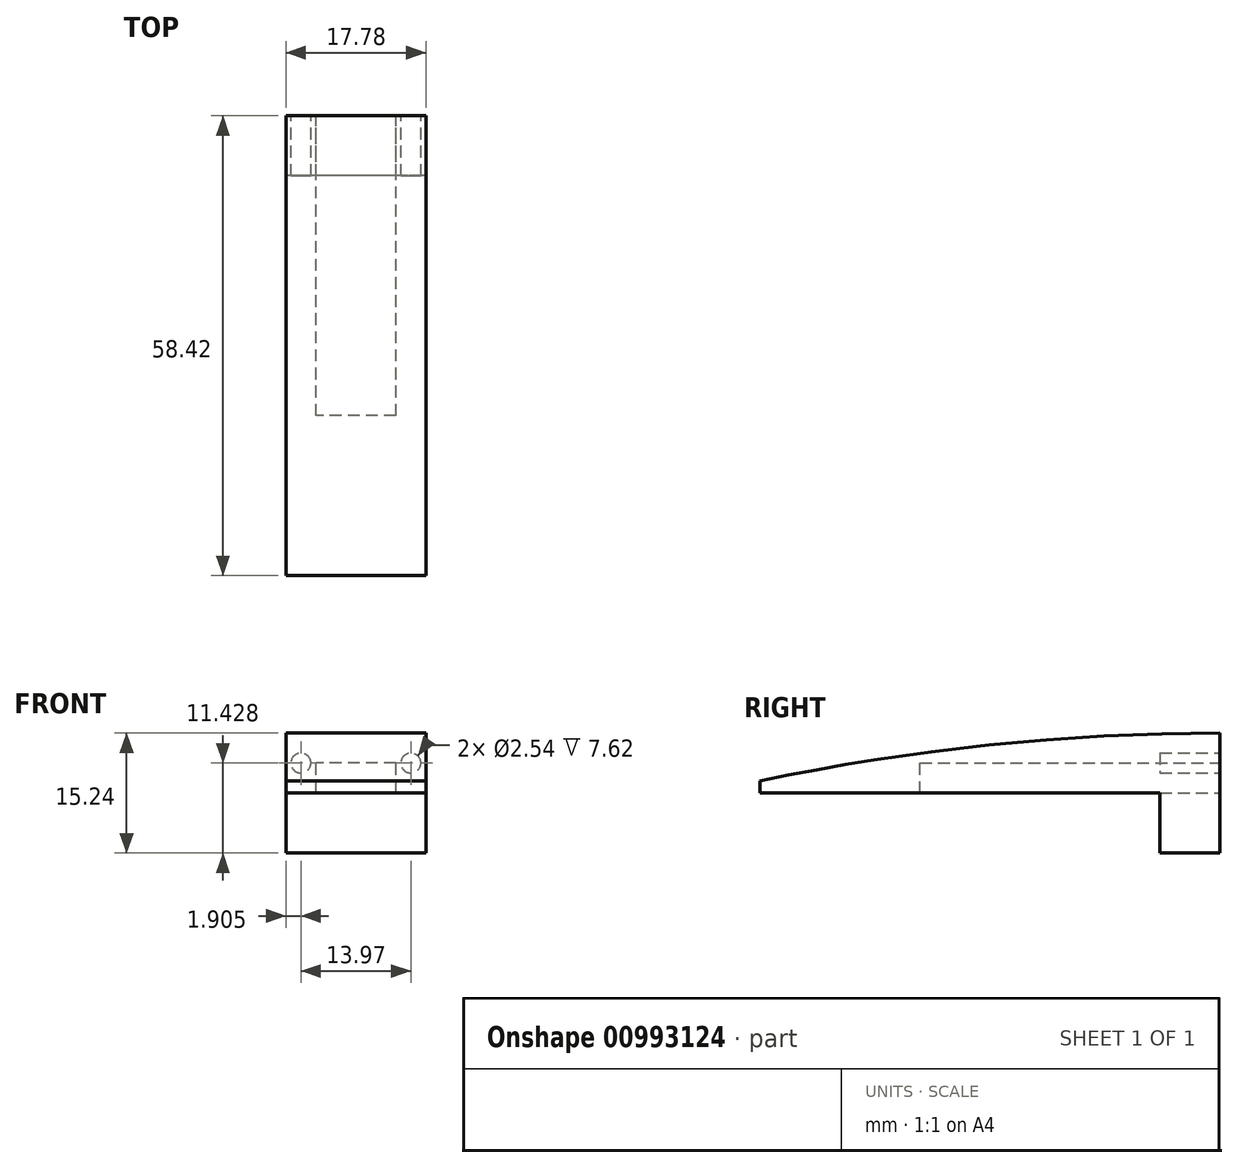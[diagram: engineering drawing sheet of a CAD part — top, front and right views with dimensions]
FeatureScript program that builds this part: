
annotation { "Feature Type Name" : "Feature", "Feature Type Description" : "" }
export const myFeature = defineFeature(function(context is Context, id is Id, definition is map)
    precondition{}
    {
        {
            var Q0;
            Q0=qCreatedBy(makeId("Right.planeOp"),FACE);
            var sketch = newSketch(context, id + "F0", { "sketchPlane" : qUnion([Q0])});
            skLineSegment(sketch, "E0.bottom", {"start": v(-45.06, 41.12) * mm, "end": v(5.74, 41.12) * mm});
            skLineSegment(sketch, "E0.top", {"start": v(-45.06, 33.5) * mm, "end": v(5.74, 33.5) * mm});
            skLineSegment(sketch, "E0.left", {"start": v(-45.06, 41.12) * mm, "end": v(-45.06, 33.5) * mm});
            skLineSegment(sketch, "E0.right", {"start": v(5.74, 41.12) * mm, "end": v(5.74, 33.5) * mm});
            skLineSegment(sketch, "E1.bottom", {"start": v(5.74, 41.12) * mm, "end": v(13.36, 41.12) * mm});
            skLineSegment(sketch, "E1.top", {"start": v(5.74, 25.88) * mm, "end": v(13.36, 25.88) * mm});
            skLineSegment(sketch, "E1.left", {"start": v(5.74, 41.12) * mm, "end": v(5.74, 25.88) * mm});
            skLineSegment(sketch, "E1.right", {"start": v(13.36, 41.12) * mm, "end": v(13.36, 25.88) * mm});
            skSolve(sketch);
        }
        {
            var Q0;
            {var subQ0=sQuery(id+"F0.wireOp",EDGE,"E0.bottom");Q0=makeQuery(id+"F0.imprint","IMPRINT",FACE,{"disambiguationData":[TD([[makeQuery(id+"F0.imprint","IMPRINT",EDGE,{"derivedFrom":subQ0}),-1.0]])]});}
            var Q1;
            {var subQ3=sQuery(id+"F0.wireOp",EDGE,"E1.bottom");Q1=makeQuery(id+"F0.imprint","IMPRINT",FACE,{"disambiguationData":[TD([[makeQuery(id+"F0.imprint","IMPRINT",EDGE,{"derivedFrom":subQ3}),-1.0]])]});}
            extrude(context, id + "F1", {"entities" : qUnion([Q0, Q1]), "depth" : 17.78 * mm, "offsetDistance" : 25.4 * mm});
        }
        {
            var Q0;
            Q0=makeQuery(id+"F1.opExtrude","CAP_FACE",FACE,{"disambiguationData":[OSD([sQuery(id+"F0.wireOp",EDGE,"E0.bottom"),sQuery(id+"F0.wireOp",EDGE,"E0.top"),sQuery(id+"F0.wireOp",EDGE,"E0.left"),sQuery(id+"F0.wireOp",EDGE,"E1.bottom"),sQuery(id+"F0.wireOp",EDGE,"E1.top"),sQuery(id+"F0.wireOp",EDGE,"E1.left"),sQuery(id+"F0.wireOp",EDGE,"E1.right")])],"isStart":false});
            var sketch = newSketch(context, id + "F2", { "sketchPlane" : qUnion([Q0])});
            skArc(sketch, "E2", {"start": v(13.36, 41.12) * mm, "mid": v(-16, 39.6) * mm, "end": v(-45.06, 35.03) * mm});
            skSolve(sketch);
        }
        {
            var Q0;
            {var subQ0=sQuery(id+"F2.wireOp",EDGE,"E2");Q0=makeQuery(id+"F2.imprint","IMPRINT",FACE,{"disambiguationData":[TD([[makeQuery(id+"F2.imprint","IMPRINT",EDGE,{"derivedFrom":subQ0}),-1.0]])]});}
            extrude(context, id + "F3", {"entities" : qUnion([Q0]), "operationType" : NewBodyOperationType.REMOVE, "oppositeDirection" : true, "depth" : 25.4 * mm, "offsetDistance" : 25.4 * mm});
        }
        {
            var Q0;
            Q0=makeQuery(id+"F1.opExtrude","SWEPT_FACE",FACE,{"disambiguationData":[OSD([sQuery(id+"F0.wireOp",EDGE,"E1.right")])]});
            var sketch = newSketch(context, id + "F4", { "sketchPlane" : qUnion([Q0])});
            skPoint(sketch, "E3.firstSnap0", {"position": v(-17.78, 33.5) * mm});
            skLineSegment(sketch, "E3.bottom", {"start": v(-13.97, 33.5) * mm, "end": v(-3.8, 33.5) * mm});
            skLineSegment(sketch, "E3.top", {"start": v(-13.97, 37.3) * mm, "end": v(-3.8, 37.3) * mm});
            skLineSegment(sketch, "E3.left", {"start": v(-13.97, 33.5) * mm, "end": v(-13.97, 37.3) * mm});
            skLineSegment(sketch, "E3.right", {"start": v(-3.8, 33.5) * mm, "end": v(-3.8, 37.3) * mm});
            skCircle(sketch, "E4", {"center": v(-15.88, 37.3) * mm, "radius": 1.27 * mm});
            skCircle(sketch, "E5", {"center": v(-1.9, 37.3) * mm, "radius": 1.27 * mm});
            skSolve(sketch);
        }
        {
            var Q0;
            Q0=makeQuery(id+"F4.imprint","IMPRINT",FACE,{"disambiguationData":[TD([[makeQuery(id+"F4.imprint","IMPRINT",EDGE,{"derivedFrom":sQuery(id+"F4.wireOp",EDGE,"E3.bottom")}),1.0]])]});
            extrude(context, id + "F5", {"entities" : qUnion([Q0]), "operationType" : NewBodyOperationType.REMOVE, "oppositeDirection" : true, "depth" : 38.1 * mm, "offsetDistance" : 25.4 * mm});
        }
        {
            var Q0;
            Q0=makeQuery(id+"F4.imprint","IMPRINT",FACE,{"disambiguationData":[TD([[makeQuery(id+"F4.imprint","IMPRINT",EDGE,{"derivedFrom":sQuery(id+"F4.wireOp",EDGE,"E5")}),1.0]])]});
            var Q1;
            Q1=makeQuery(id+"F4.imprint","IMPRINT",FACE,{"disambiguationData":[TD([[makeQuery(id+"F4.imprint","IMPRINT",EDGE,{"derivedFrom":sQuery(id+"F4.wireOp",EDGE,"E4")}),1.0]])]});
            extrude(context, id + "F6", {"entities" : qUnion([Q0, Q1]), "operationType" : NewBodyOperationType.REMOVE, "oppositeDirection" : true, "depth" : 7.62 * mm, "offsetDistance" : 25.4 * mm});
        }
    });
